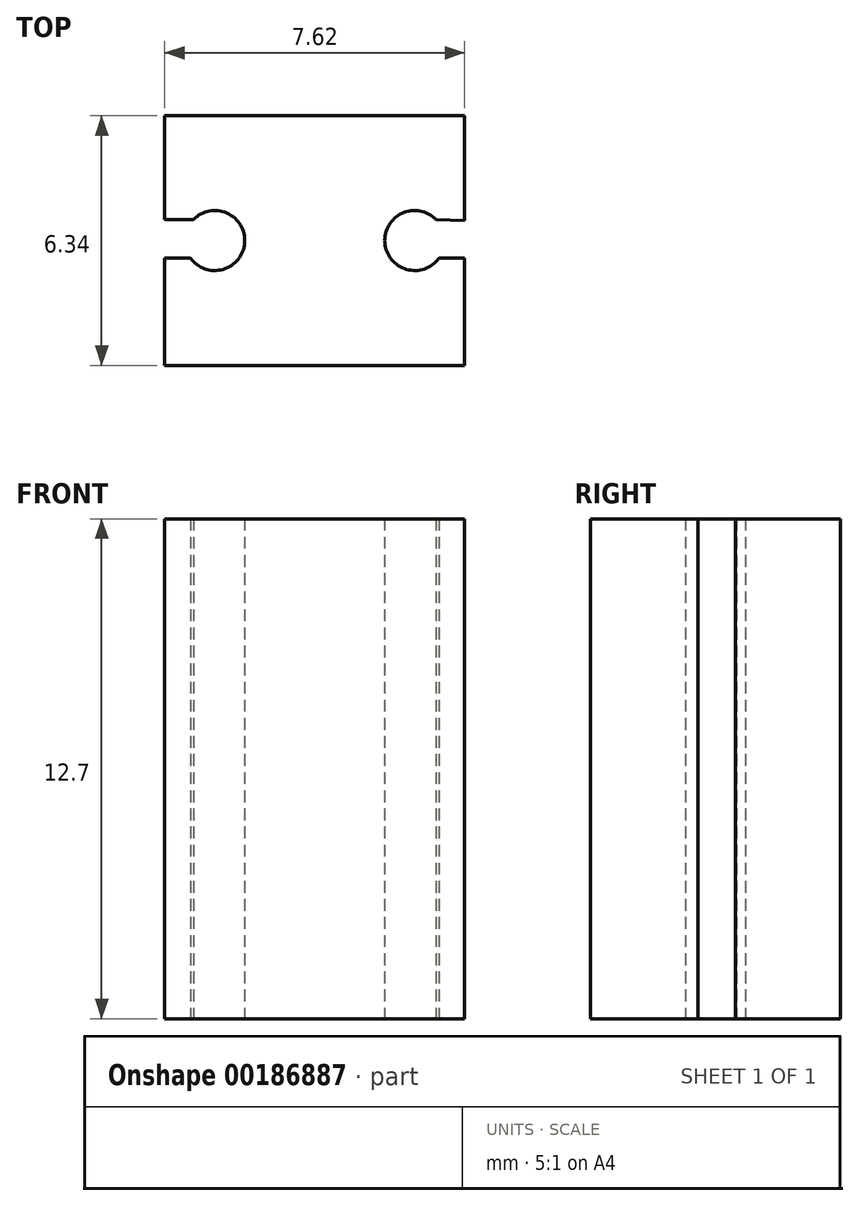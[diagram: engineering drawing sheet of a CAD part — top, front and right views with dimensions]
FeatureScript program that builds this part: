
annotation { "Feature Type Name" : "Feature", "Feature Type Description" : "" }
export const myFeature = defineFeature(function(context is Context, id is Id, definition is map)
    precondition{}
    {
        {
            var Q0;
            Q0=qCreatedBy(makeId("Top.planeOp"),FACE);
            var sketch = newSketch(context, id + "F0", { "sketchPlane" : qUnion([Q0])});
            skLineSegment(sketch, "E0.bottom", {"start": v(-3.81, -3.17) * mm, "end": v(3.81, -3.17) * mm});
            skLineSegment(sketch, "E0.top", {"start": v(-3.81, 3.17) * mm, "end": v(3.81, 3.17) * mm});
            skLineSegment(sketch, "E0.left", {"start": v(-3.81, -3.17) * mm, "end": v(-3.81, 3.17) * mm});
            skLineSegment(sketch, "E0.right", {"start": v(3.81, -3.17) * mm, "end": v(3.81, 3.17) * mm});
            skPoint(sketch, "E0.middle", {"position": v(0, 0) * mm});
            skPoint(sketch, "E1", {"position": v(2.54, 0) * mm});
            skPoint(sketch, "E2", {"position": v(-2.54, 0) * mm});
            skCircle(sketch, "E3", {"center": v(2.54, 0) * mm, "radius": 0.76 * mm});
            skLineSegment(sketch, "E4.direction1", {"start": v(4.06, 0) * mm, "end": v(-4.32, 0) * mm, "construction": true});
            skCircle(sketch, "E5", {"center": v(-2.54, 0) * mm, "radius": 0.76 * mm});
            skPoint(sketch, "E6", {"position": v(3.3, 0) * mm});
            skPoint(sketch, "E7", {"position": v(3.08, 0.54) * mm});
            skPoint(sketch, "E8", {"position": v(3.16, -0.45) * mm});
            skPoint(sketch, "E9", {"position": v(-1.92, -0.45) * mm});
            skPoint(sketch, "E10", {"position": v(-2, 0.54) * mm});
            skPoint(sketch, "E11", {"position": v(-3.08, 0.54) * mm});
            skPoint(sketch, "E12", {"position": v(-3.16, -0.45) * mm});
            skPoint(sketch, "E13", {"position": v(-3.81, -0.45) * mm});
            skPoint(sketch, "E14", {"position": v(-3.81, 0.54) * mm});
            skLineSegment(sketch, "E15", {"start": v(-3.81, 0.54) * mm, "end": v(-3.08, 0.54) * mm});
            skLineSegment(sketch, "E16", {"start": v(-3.16, -0.45) * mm, "end": v(-3.81, -0.45) * mm});
            skLineSegment(sketch, "E17", {"start": v(-3.81, -0.45) * mm, "end": v(-3.81, 0.54) * mm});
            skLineSegment(sketch, "E18", {"start": v(3.08, 0.54) * mm, "end": v(3.81, 0.5) * mm});
            skLineSegment(sketch, "E19", {"start": v(3.81, -0.45) * mm, "end": v(3.16, -0.45) * mm});
            skLineSegment(sketch, "E20", {"start": v(3.81, 0.5) * mm, "end": v(3.81, -0.45) * mm});
            skArc(sketch, "E21", {"start": v(-3.08, 0.54) * mm, "mid": v(-3.29, 0.06) * mm, "end": v(-3.16, -0.45) * mm});
            skArc(sketch, "E22", {"start": v(3.16, -0.45) * mm, "mid": v(3.3, 0.06) * mm, "end": v(3.08, 0.54) * mm});
            skPoint(sketch, "E23", {"position": v(-3.29, -0.06) * mm});
            skPoint(sketch, "E23.positionSnap0", {"position": v(-3.29, 0.06) * mm});
            skSolve(sketch);
        }
        {
            var Q0;
            {var subQ4=sQuery(id+"F0.wireOp",EDGE,"E0.bottom");Q0=makeQuery(id+"F0.imprint","IMPRINT",FACE,{"disambiguationData":[TD([[makeQuery(id+"F0.imprint","IMPRINT",EDGE,{"derivedFrom":subQ4}),1.0]])]});}
            extrude(context, id + "F1", {"entities" : qUnion([Q0]), "depth" : 12.7 * mm});
        }
    });
